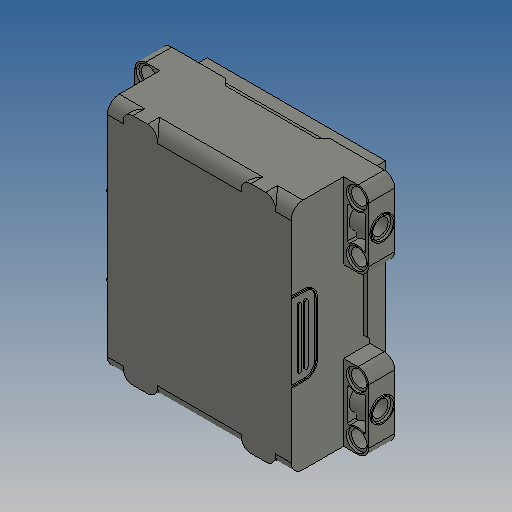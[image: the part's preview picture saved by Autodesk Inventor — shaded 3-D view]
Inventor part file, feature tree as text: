
AUTODESK INVENTOR PART (.ipt)
format: ipt  version: 2025 (Build 290162010, 162A)  size: 695,808 bytes
history: native  units: mm
features: move_body x8, direct_edit x4, fillet x2, delete_face x1, extrude x1, sketch x1, imported_body x1
ambient origin geometry x8: Origin, YZ Plane, XZ Plane, XY Plane, X Axis, Y Axis, Z Axis, Center Point
bodies: Volumenkörper1 (feature_tree)
feature tree (18):
  direct_edit  "Direktbearbeitung1"
  direct_edit  "Direktbearbeitung2"
  direct_edit  "Direktbearbeitung3"
  delete_face  "Fläche löschen1"
  fillet  "Rundung1"  [1 undecoded]
  direct_edit  "Direktbearbeitung4"
  fillet  "Rundung2"  Radius=0.6mm
  extrude  "Extrusion1"  Depth=10.0mm TaperAngle=0.0deg
  sketch  "Skizze1"  dims[d0=0.0mm d1=0.0mm d2=-0.4mm d3=0.0mm d4=0.0mm d5=-0.4mm d6=0.0mm d7=0.0mm d8=0.6mm d9=0.0mm d10=0.0mm d11=0.8mm d12=0.8mm d13=0.0mm d14=0.0mm d15=0.2mm d16=0.0mm d17=0.0mm d18=0.2mm d19=0.0mm d20=0.4mm d21=0.0mm d22=0.0mm d23=0.4mm d24=0.0mm d25=0.4mm d26=3.0mm d27=10.5mm d28=36.0mm d29=10.0mm d30=10.0mm d31=10.0mm d32=0.0mm]
  imported_body  "Basis1"
  move_body  "Verschieben1"
  move_body  "Verschieben2"
  move_body  "Verschieben3"
  move_body  "Verschieben4"
  move_body  "Verschieben5"
  move_body  "Verschieben6"
  move_body  "Verschieben7"
  move_body  "Verschieben8"
note: 1 required parameter value undecoded (feature->parameter linkage not recoverable at this tier; creation-order binding heuristic only, values carry confidence <= 0.55)
